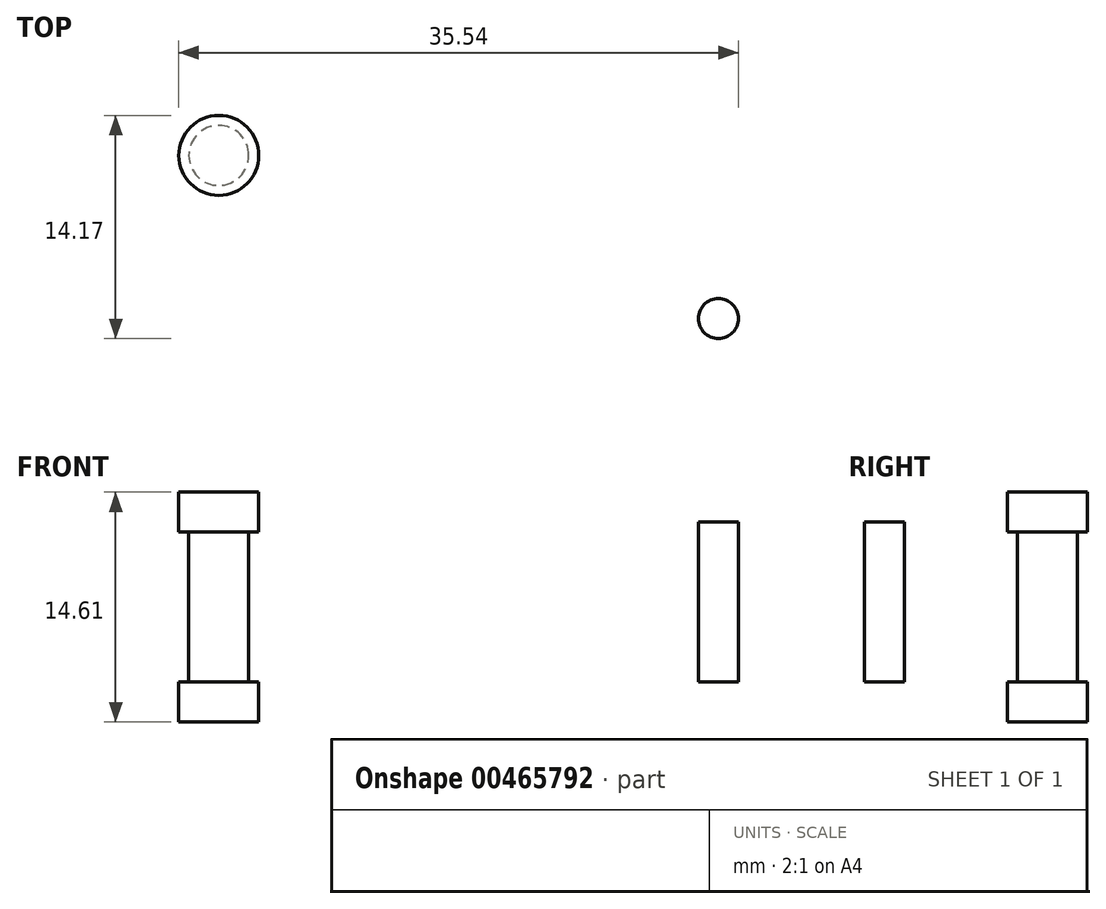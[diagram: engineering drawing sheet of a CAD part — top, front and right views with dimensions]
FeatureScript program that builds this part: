
annotation { "Feature Type Name" : "Feature", "Feature Type Description" : "" }
export const myFeature = defineFeature(function(context is Context, id is Id, definition is map)
    precondition{}
    {
        {
            var Q0;
            Q0=qCreatedBy(makeId("Top.planeOp"),FACE);
            var sketch = newSketch(context, id + "F0", { "sketchPlane" : qUnion([Q0])});
            skCircle(sketch, "E0", {"center": v(0, 0) * mm, "radius": 2.54 * mm});
            skCircle(sketch, "E1", {"center": v(0, 0) * mm, "radius": 1.9 * mm});
            skSolve(sketch);
        }
        {
            var Q0;
            Q0=makeQuery(id+"F0.imprint","IMPRINT",FACE,{"disambiguationData":[TD([[makeQuery(id+"F0.imprint","IMPRINT",EDGE,{"derivedFrom":sQuery(id+"F0.wireOp",EDGE,"E1")}),1.0]])]});
            var Q1;
            Q1=makeQuery(id+"F0.imprint","IMPRINT",FACE,{"disambiguationData":[TD([[makeQuery(id+"F0.imprint","IMPRINT",EDGE,{"derivedFrom":sQuery(id+"F0.wireOp",EDGE,"E0")}),1.0]])]});
            extrude(context, id + "F1", {"entities" : qUnion([Q0, Q1]), "oppositeDirection" : true, "depth" : 2.54 * mm});
        }
        {
            var Q0;
            Q0=makeQuery(id+"F0.imprint","IMPRINT",FACE,{"disambiguationData":[TD([[makeQuery(id+"F0.imprint","IMPRINT",EDGE,{"derivedFrom":sQuery(id+"F0.wireOp",EDGE,"E1")}),1.0]])]});
            extrude(context, id + "F2", {"entities" : qUnion([Q0]), "operationType" : NewBodyOperationType.ADD, "depth" : 9.52 * mm});
        }
        {
            var Q0;
            Q0=makeQuery(id+"F2.opExtrude","CAP_FACE",FACE,{"disambiguationData":[OSD([sQuery(id+"F0.wireOp",EDGE,"E1")])],"isStart":false});
            var sketch = newSketch(context, id + "F3", { "sketchPlane" : qUnion([Q0])});
            skCircle(sketch, "E2", {"center": v(0, 0) * mm, "radius": 2.54 * mm});
            skSolve(sketch);
        }
        {
            var Q0;
            Q0=qSketchRegion(id+"F3",true);
            extrude(context, id + "F4", {"entities" : qUnion([Q0]), "operationType" : NewBodyOperationType.ADD, "depth" : 2.54 * mm});
        }
        {
            var Q0;
            Q0=qCreatedBy(makeId("Top.planeOp"),FACE);
            var sketch = newSketch(context, id + "F5", { "sketchPlane" : qUnion([Q0])});
            skCircle(sketch, "E3", {"center": v(31.73, -10.36) * mm, "radius": 1.27 * mm});
            skSolve(sketch);
        }
        {
            var Q0;
            Q0=makeQuery(id+"F5.imprint","IMPRINT",FACE,{"disambiguationData":[TD([[makeQuery(id+"F5.imprint","IMPRINT",EDGE,{"derivedFrom":sQuery(id+"F5.wireOp",EDGE,"E3")}),1.0]])]});
            extrude(context, id + "F6", {"entities" : qUnion([Q0]), "depth" : 10.16 * mm});
        }
    });
